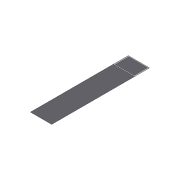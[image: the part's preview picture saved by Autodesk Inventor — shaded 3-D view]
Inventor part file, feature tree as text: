
AUTODESK INVENTOR PART (.ipt)
format: ipt  version: 2012 (Build 160160000, 160)  size: 72,192 bytes
history: native  units: in
note: dims shown in document units (in); Inventor stores cm internally (conversion verified against a paired STEP export)
features: extrude x1, shell x1, sketch x1
ambient origin geometry x8: Origin, YZ Plane, XZ Plane, XY Plane, X Axis, Y Axis, Z Axis, Center Point
bodies: Solid1 (feature_tree)
feature tree (3):
  extrude  "Extrusion1"  TaperAngle=45.0deg  [1 undecoded]
  shell  "Shell1"  Thickness=5.5in
  sketch  "Sketch1"  dims[d1=1.0in d2=45.0deg d3=5.5in d4=1.0in d5=0.0in d6=0.0625in]
note: 1 required parameter value undecoded (feature->parameter linkage not recoverable at this tier; creation-order binding heuristic only, values carry confidence <= 0.55)
